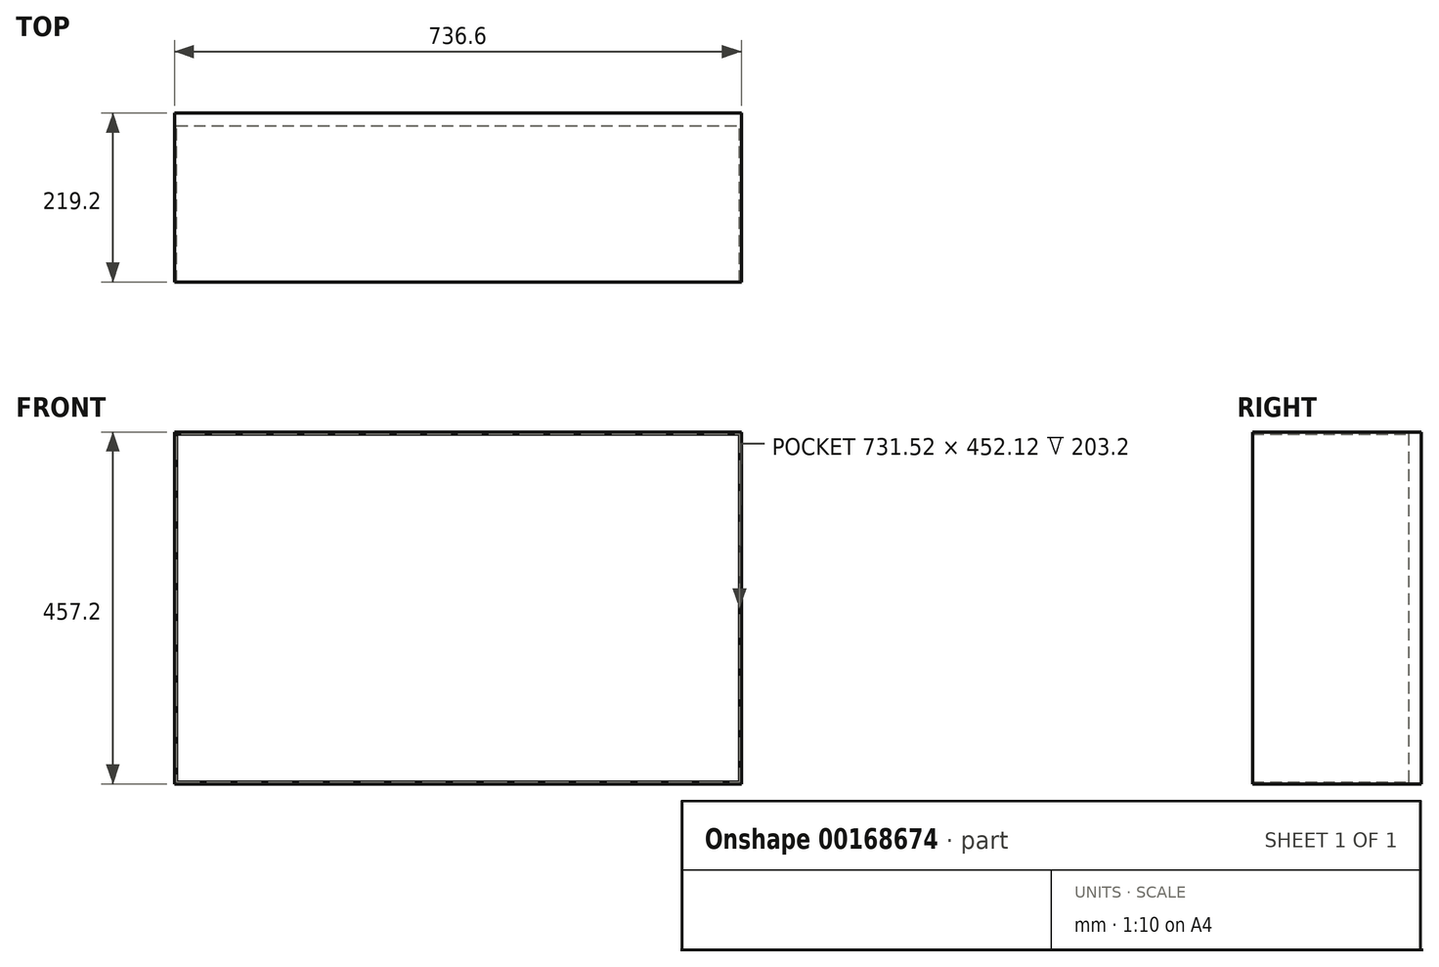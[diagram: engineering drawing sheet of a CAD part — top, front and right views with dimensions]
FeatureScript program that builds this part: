
annotation { "Feature Type Name" : "Feature", "Feature Type Description" : "" }
export const myFeature = defineFeature(function(context is Context, id is Id, definition is map)
    precondition{}
    {
        {
            var Q0;
            Q0=qCreatedBy(makeId("Front.planeOp"),FACE);
            var sketch = newSketch(context, id + "F0", { "sketchPlane" : qUnion([Q0])});
            skLineSegment(sketch, "E0.bottom", {"start": v(0, 0) * mm, "end": v(736.6, 0) * mm});
            skLineSegment(sketch, "E0.top", {"start": v(0, 457.2) * mm, "end": v(736.6, 457.2) * mm});
            skLineSegment(sketch, "E0.left", {"start": v(0, 0) * mm, "end": v(0, 457.2) * mm});
            skLineSegment(sketch, "E0.right", {"start": v(736.6, 0) * mm, "end": v(736.6, 457.2) * mm});
            skPoint(sketch, "E1", {"position": v(50.8, 406.4) * mm});
            skSolve(sketch);
        }
        {
            var Q0;
            Q0=qCreatedBy(makeId("Front.planeOp"),FACE);
            var sketch = newSketch(context, id + "F1", { "sketchPlane" : qUnion([Q0])});
            skLineSegment(sketch, "E2.bottom", {"start": v(0, 0) * mm, "end": v(736.6, 0) * mm});
            skLineSegment(sketch, "E2.top", {"start": v(0, 457.2) * mm, "end": v(736.6, 457.2) * mm});
            skLineSegment(sketch, "E2.left", {"start": v(0, 0) * mm, "end": v(0, 457.2) * mm});
            skLineSegment(sketch, "E2.right", {"start": v(736.6, 0) * mm, "end": v(736.6, 457.2) * mm});
            skSolve(sketch);
        }
        {
            var Q0;
            Q0 = qSketchRegion(id + "F0", true);
            extrude(context, id + "F2", {"entities" : qUnion([Q0]), "depth" : 219.2 * mm});
        }
        {
            var Q0;
            Q0=makeQuery(id+"F2.opExtrude","CAP_FACE",FACE,{"disambiguationData":[OSD([sQuery(id+"F0.wireOp",EDGE,"E0.bottom"),sQuery(id+"F0.wireOp",EDGE,"E0.top"),sQuery(id+"F0.wireOp",EDGE,"E0.left"),sQuery(id+"F0.wireOp",EDGE,"E0.right")])],"isStart":false});
            shell(context, id + "F3", {"entities" : qUnion([Q0]), "thickness" : 2.54 * mm});
        }
        {
            var Q0;
            Q0 = qSketchRegion(id + "F1", true);
            extrude(context, id + "F4", {"entities" : qUnion([Q0]), "operationType" : NewBodyOperationType.ADD, "depth" : 16 * mm});
        }
    });
